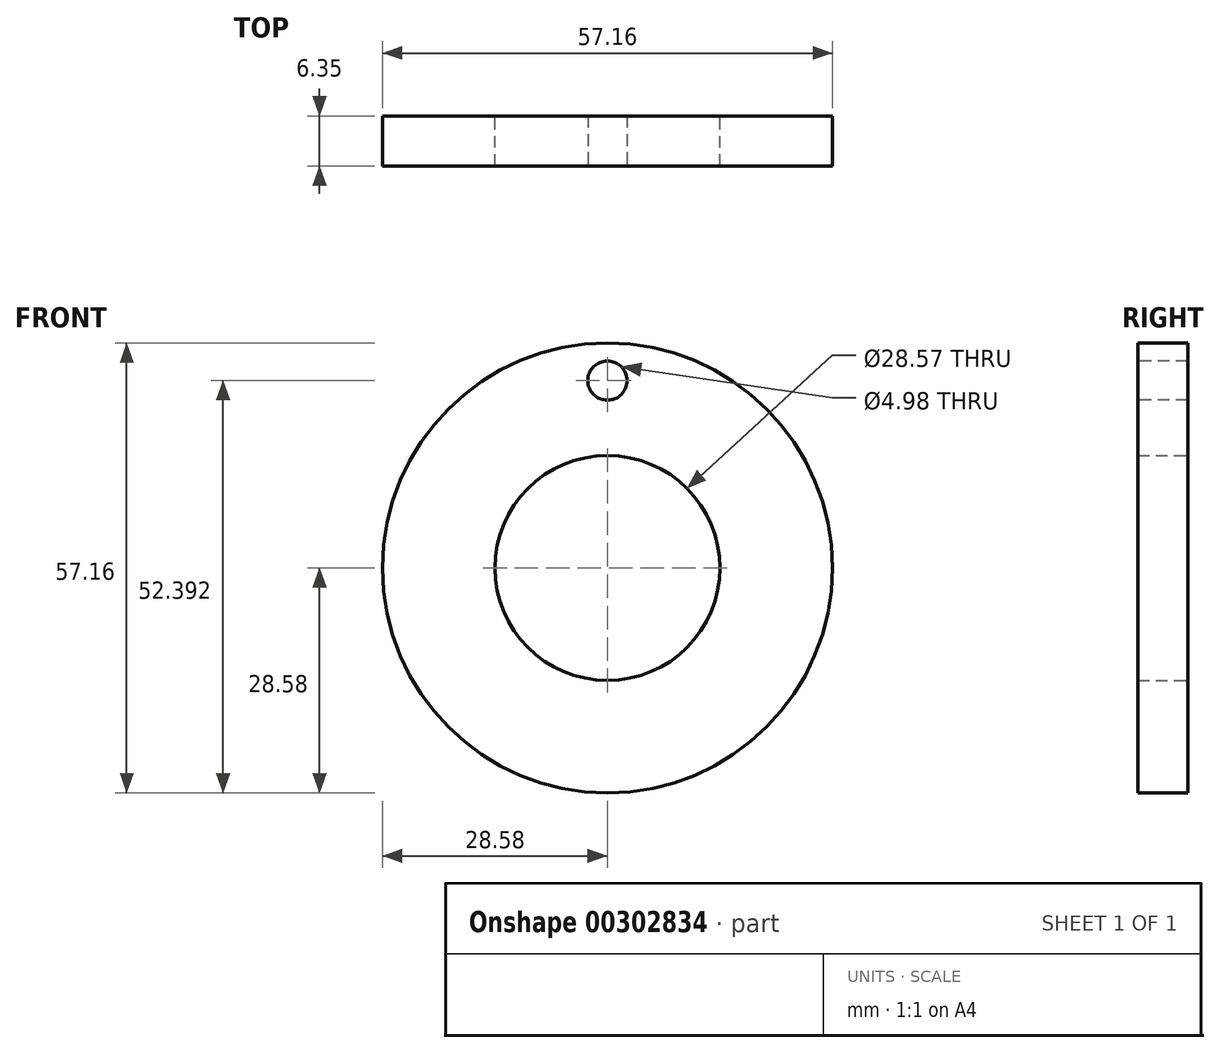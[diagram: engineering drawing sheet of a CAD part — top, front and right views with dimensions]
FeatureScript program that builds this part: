
annotation { "Feature Type Name" : "Feature", "Feature Type Description" : "" }
export const myFeature = defineFeature(function(context is Context, id is Id, definition is map)
    precondition{}
    {
        {
            var Q0;
            Q0=qCreatedBy(makeId("Front.planeOp"),FACE);
            var sketch = newSketch(context, id + "F0", { "sketchPlane" : qUnion([Q0])});
            skCircle(sketch, "E0", {"center": v(0, 0) * mm, "radius": 28.58 * mm});
            skCircle(sketch, "E1", {"center": v(0, 0) * mm, "radius": 14.29 * mm});
            skSolve(sketch);
        }
        {
            var Q0;
            Q0=qSketchRegion(id+"F0",true);
            extrude(context, id + "F1", {"entities" : qUnion([Q0]), "depth" : 6.35 * mm});
        }
        {
            var Q0;
            Q0=makeQuery(id+"F1.opExtrude","CAP_FACE",FACE,{"disambiguationData":[OSD([sQuery(id+"F0.wireOp",EDGE,"E0"),sQuery(id+"F0.wireOp",EDGE,"E1")])],"isStart":false});
            var sketch = newSketch(context, id + "F2", { "sketchPlane" : qUnion([Q0])});
            skCircle(sketch, "E2", {"center": v(0, 23.81) * mm, "radius": 2.49 * mm});
            skSolve(sketch);
        }
        {
            var Q0;
            Q0=qSketchRegion(id+"F2",true);
            extrude(context, id + "F3", {"entities" : qUnion([Q0]), "operationType" : NewBodyOperationType.REMOVE, "endBound" : BoundingType.THROUGH_ALL, "oppositeDirection" : true, "depth" : 25.4 * mm});
        }
    });
